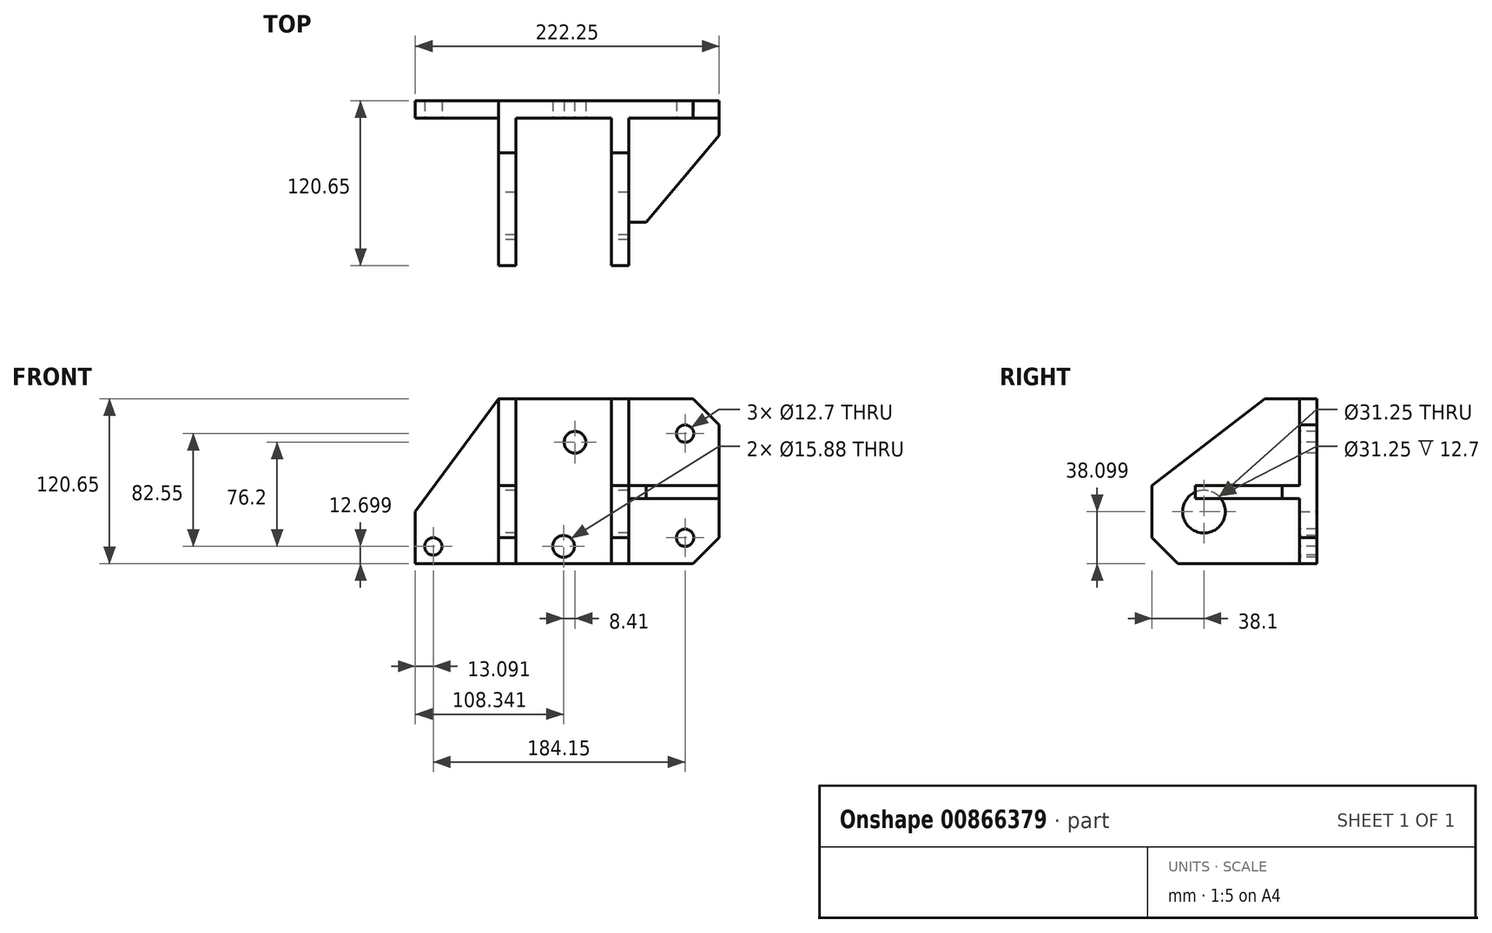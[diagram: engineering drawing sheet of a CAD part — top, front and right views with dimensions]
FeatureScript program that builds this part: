
annotation { "Feature Type Name" : "Feature", "Feature Type Description" : "" }
export const myFeature = defineFeature(function(context is Context, id is Id, definition is map)
    precondition{}
    {
        {
            var Q0;
            Q0=qCreatedBy(makeId("Front.planeOp"),FACE);
            var sketch = newSketch(context, id + "F0", { "sketchPlane" : qUnion([Q0])});
            skLineSegment(sketch, "E0.bottom", {"start": v(-58.45, 64.57) * mm, "end": v(103.08, 64.57) * mm});
            skLineSegment(sketch, "E0.right", {"start": v(103.08, 64.57) * mm, "end": v(103.08, -56.08) * mm});
            skLineSegment(sketch, "E1", {"start": v(-58.45, 64.57) * mm, "end": v(-119.17, -17.98) * mm});
            skLineSegment(sketch, "E2", {"start": v(-119.17, -17.98) * mm, "end": v(-119.17, -56.08) * mm});
            skLineSegment(sketch, "E3", {"start": v(-119.17, -56.08) * mm, "end": v(103.08, -56.08) * mm});
            skSolve(sketch);
        }
        {
            var Q0;
            Q0 = qSketchRegion(id + "F0", true);
            extrude(context, id + "F1", {"entities" : qUnion([Q0]), "depth" : 12.7 * mm, "offsetDistance" : 25.4 * mm});
        }
        {
            var Q0;
            Q0=makeQuery(id+"F1.opExtrude","SWEPT_EDGE",EDGE,{"disambiguationData":[OSD([sQuery(id+"F0.wireOp",EDGE,"E0.right"),sQuery(id+"F0.wireOp",EDGE,"E3")])]});
            var Q1;
            Q1=makeQuery(id+"F1.opExtrude","SWEPT_EDGE",EDGE,{"disambiguationData":[OSD([sQuery(id+"F0.wireOp",EDGE,"E0.bottom"),sQuery(id+"F0.wireOp",EDGE,"E0.right")])]});
            chamfer(context, id + "F2", {"entities" : qUnion([Q0, Q1]), "width" : 19.05 * mm, "tangentPropagation" : true});
        }
        {
            var Q0;
            Q0=makeQuery(id+"F1.opExtrude","CAP_FACE",FACE,{"disambiguationData":[OSD([sQuery(id+"F0.wireOp",EDGE,"E0.bottom"),sQuery(id+"F0.wireOp",EDGE,"E0.right"),sQuery(id+"F0.wireOp",EDGE,"E1"),sQuery(id+"F0.wireOp",EDGE,"E2"),sQuery(id+"F0.wireOp",EDGE,"E3")])],"isStart":false});
            var sketch = newSketch(context, id + "F3", { "sketchPlane" : qUnion([Q0])});
            skLineSegment(sketch, "E4", {"start": v(-58.45, 64.57) * mm, "end": v(-58.45, -56.08) * mm});
            skLineSegment(sketch, "E5", {"start": v(-45.75, 64.57) * mm, "end": v(-45.75, -56.08) * mm});
            skLineSegment(sketch, "E6", {"start": v(24.1, 64.57) * mm, "end": v(24.1, -56.08) * mm});
            skLineSegment(sketch, "E7", {"start": v(24.1, -56.08) * mm, "end": v(36.8, -56.08) * mm});
            skLineSegment(sketch, "E8", {"start": v(36.8, -56.08) * mm, "end": v(36.8, 64.57) * mm});
            skLineSegment(sketch, "E9", {"start": v(36.8, 64.57) * mm, "end": v(24.1, 64.57) * mm});
            skLineSegment(sketch, "E10", {"start": v(-58.45, 64.57) * mm, "end": v(-45.75, 64.57) * mm});
            skLineSegment(sketch, "E11", {"start": v(-58.45, -56.08) * mm, "end": v(-45.75, -56.08) * mm});
            skLineSegment(sketch, "E12", {"start": v(36.8, -8.46) * mm, "end": v(103.08, -8.46) * mm});
            skLineSegment(sketch, "E13", {"start": v(103.08, -8.46) * mm, "end": v(103.08, 1.07) * mm});
            skLineSegment(sketch, "E14", {"start": v(103.08, 1.07) * mm, "end": v(36.8, 1.07) * mm});
            skCircle(sketch, "E15", {"center": v(78.07, -37.03) * mm, "radius": 6.35 * mm});
            skCircle(sketch, "E16", {"center": v(78.07, 39.17) * mm, "radius": 6.35 * mm});
            skCircle(sketch, "E17", {"center": v(-106.08, -43.38) * mm, "radius": 6.35 * mm});
            skCircle(sketch, "E18", {"center": v(-2.42, 32.82) * mm, "radius": 7.94 * mm});
            skCircle(sketch, "E19", {"center": v(-10.83, -43.38) * mm, "radius": 7.94 * mm});
            skSolve(sketch);
        }
        {
            var Q0;
            Q0=makeQuery(id+"F3.imprint","IMPRINT",FACE,{"disambiguationData":[TD([[makeQuery(id+"F3.imprint","IMPRINT",EDGE,{"derivedFrom":sQuery(id+"F3.wireOp",EDGE,"E15")}),1.0]])]});
            var Q1;
            Q1=makeQuery(id+"F3.imprint","IMPRINT",FACE,{"disambiguationData":[TD([[makeQuery(id+"F3.imprint","IMPRINT",EDGE,{"derivedFrom":sQuery(id+"F3.wireOp",EDGE,"E16")}),1.0]])]});
            var Q2;
            Q2=makeQuery(id+"F3.imprint","IMPRINT",FACE,{"disambiguationData":[TD([[makeQuery(id+"F3.imprint","IMPRINT",EDGE,{"derivedFrom":sQuery(id+"F3.wireOp",EDGE,"E18")}),1.0]])]});
            var Q3;
            Q3=makeQuery(id+"F3.imprint","IMPRINT",FACE,{"disambiguationData":[TD([[makeQuery(id+"F3.imprint","IMPRINT",EDGE,{"derivedFrom":sQuery(id+"F3.wireOp",EDGE,"E19")}),1.0]])]});
            var Q4;
            Q4=makeQuery(id+"F3.imprint","IMPRINT",FACE,{"disambiguationData":[TD([[makeQuery(id+"F3.imprint","IMPRINT",EDGE,{"derivedFrom":sQuery(id+"F3.wireOp",EDGE,"E17")}),1.0]])]});
            extrude(context, id + "F4", {"entities" : qUnion([Q0, Q1, Q2, Q3, Q4]), "operationType" : NewBodyOperationType.REMOVE, "oppositeDirection" : true, "depth" : 25.4 * mm, "offsetDistance" : 25.4 * mm});
        }
        {
            var Q0;
            Q0=makeQuery(id+"F3.imprint","IMPRINT",FACE,{"disambiguationData":[TD([[makeQuery(id+"F3.imprint","IMPRINT",EDGE,{"derivedFrom":sQuery(id+"F3.wireOp",EDGE,"E4")}),1.0]])]});
            var Q1;
            Q1=makeQuery(id+"F3.imprint","IMPRINT",FACE,{"disambiguationData":[TD([[makeQuery(id+"F3.imprint","IMPRINT",EDGE,{"derivedFrom":sQuery(id+"F3.wireOp",EDGE,"E6")}),1.0]])]});
            extrude(context, id + "F5", {"entities" : qUnion([Q0, Q1]), "operationType" : NewBodyOperationType.ADD, "depth" : 107.95 * mm, "offsetDistance" : 25.4 * mm});
        }
        {
            var Q0;
            Q0=makeQuery(id+"F5.opExtrude","CAP_EDGE",EDGE,{"disambiguationData":[OSD([sQuery(id+"F3.wireOp",EDGE,"E11")])],"isStart":false});
            var Q1;
            Q1=makeQuery(id+"F5.opExtrude","CAP_EDGE",EDGE,{"disambiguationData":[OSD([sQuery(id+"F3.wireOp",EDGE,"E7")])],"isStart":false});
            chamfer(context, id + "F6", {"entities" : qUnion([Q0, Q1]), "width" : 19.05 * mm, "tangentPropagation" : true});
        }
        {
            var Q0;
            Q0=makeQuery(id+"F5.opExtrude","SWEPT_FACE",FACE,{"disambiguationData":[OSD([sQuery(id+"F3.wireOp",EDGE,"E4")])]});
            var sketch = newSketch(context, id + "F7", { "sketchPlane" : qUnion([Q0])});
            skLineSegment(sketch, "E20", {"start": v(120.65, 1.07) * mm, "end": v(38.1, 64.57) * mm});
            skCircle(sketch, "E21", {"center": v(82.55, -17.98) * mm, "radius": 15.63 * mm});
            skSolve(sketch);
        }
        {
            var Q0;
            {var subQ0=sQuery(id+"F7.wireOp",EDGE,"E20");Q0=makeQuery(id+"F7.imprint","IMPRINT",FACE,{"disambiguationData":[TD([[makeQuery(id+"F7.imprint","IMPRINT",EDGE,{"derivedFrom":subQ0}),-1.0]])]});}
            extrude(context, id + "F8", {"entities" : qUnion([Q0]), "operationType" : NewBodyOperationType.REMOVE, "oppositeDirection" : true, "depth" : 193.55 * mm, "offsetDistance" : 25.4 * mm});
        }
        {
            var Q0;
            Q0=makeQuery(id+"F7.imprint","IMPRINT",FACE,{"disambiguationData":[TD([[makeQuery(id+"F7.imprint","IMPRINT",EDGE,{"derivedFrom":sQuery(id+"F7.wireOp",EDGE,"E21")}),1.0]])]});
            extrude(context, id + "F9", {"entities" : qUnion([Q0]), "operationType" : NewBodyOperationType.REMOVE, "endBound" : BoundingType.THROUGH_ALL, "oppositeDirection" : true, "depth" : 25.4 * mm, "offsetDistance" : 25.4 * mm});
        }
        {
            var Q0;
            {var subQ0=sQuery(id+"F3.wireOp",EDGE,"E12");Q0=makeQuery(id+"F3.imprint","IMPRINT",FACE,{"disambiguationData":[TD([[makeQuery(id+"F3.imprint","IMPRINT",EDGE,{"derivedFrom":subQ0}),1.0]])]});}
            extrude(context, id + "F10", {"entities" : qUnion([Q0]), "operationType" : NewBodyOperationType.ADD, "depth" : 76.2 * mm, "offsetDistance" : 25.4 * mm});
        }
        {
            var Q0;
            Q0=makeQuery(id+"F10.opExtrude","SWEPT_FACE",FACE,{"disambiguationData":[OSD([sQuery(id+"F3.wireOp",EDGE,"E14")])]});
            var sketch = newSketch(context, id + "F11", { "sketchPlane" : qUnion([Q0])});
            skLineSegment(sketch, "E22", {"start": v(49.5, -88.9) * mm, "end": v(103.08, -25.4) * mm});
            skSolve(sketch);
        }
        {
            var Q0;
            {var subQ0=sQuery(id+"F11.wireOp",EDGE,"E22");Q0=makeQuery(id+"F11.imprint","IMPRINT",FACE,{"disambiguationData":[TD([[makeQuery(id+"F11.imprint","IMPRINT",EDGE,{"derivedFrom":subQ0}),-1.0]])]});}
            extrude(context, id + "F12", {"entities" : qUnion([Q0]), "operationType" : NewBodyOperationType.REMOVE, "endBound" : BoundingType.THROUGH_ALL, "oppositeDirection" : true, "depth" : 25.4 * mm, "offsetDistance" : 25.4 * mm});
        }
    });
